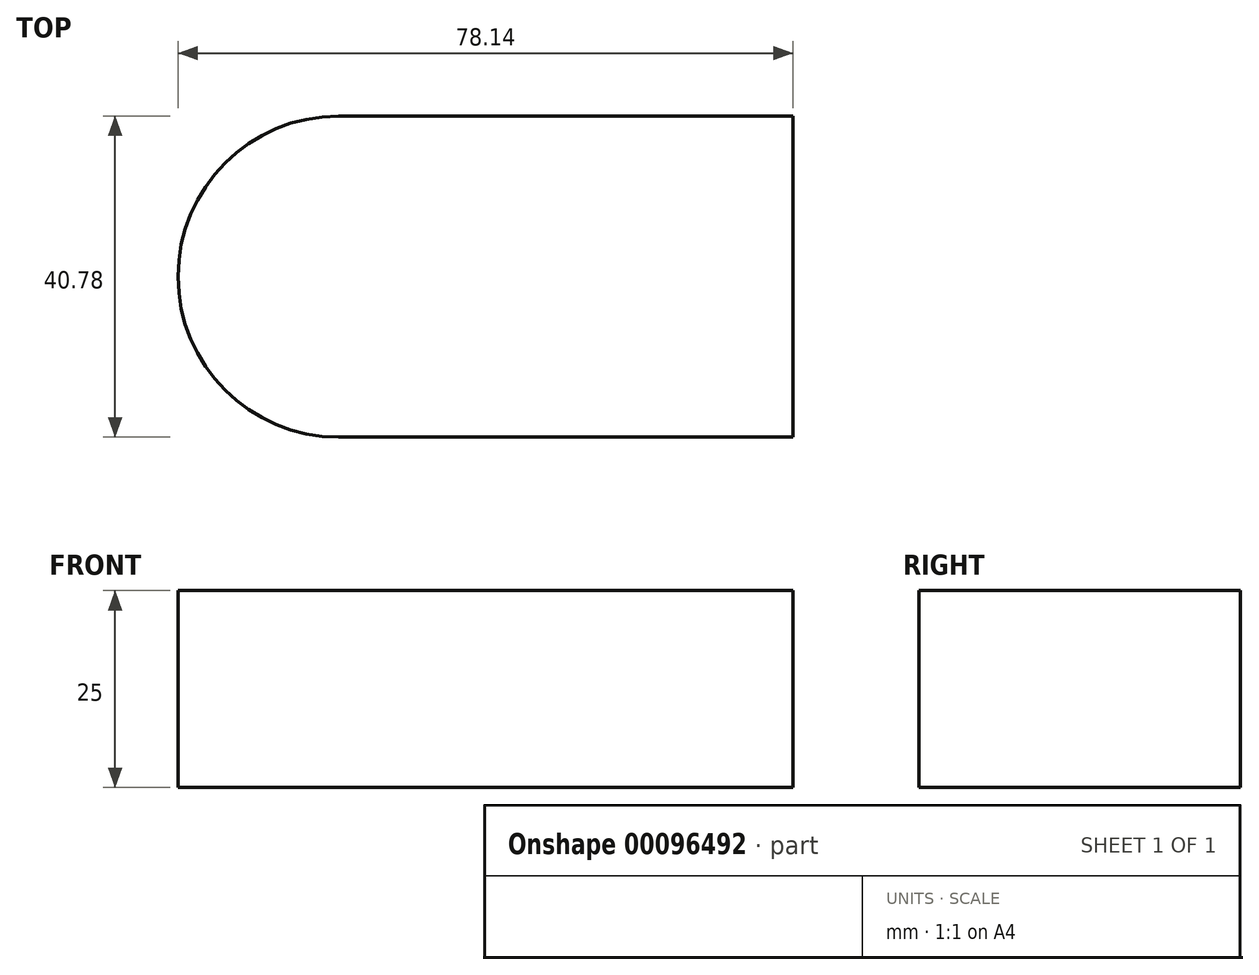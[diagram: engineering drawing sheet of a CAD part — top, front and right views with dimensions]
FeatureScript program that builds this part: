
annotation { "Feature Type Name" : "Feature", "Feature Type Description" : "" }
export const myFeature = defineFeature(function(context is Context, id is Id, definition is map)
    precondition{}
    {
        {
            var Q0;
            Q0=qCreatedBy(makeId("Top.planeOp"),FACE);
            var sketch = newSketch(context, id + "F0", { "sketchPlane" : qUnion([Q0])});
            skLineSegment(sketch, "E0.bottom", {"start": v(5, 0) * mm, "end": v(57.75, 0) * mm});
            skLineSegment(sketch, "E0.top", {"start": v(5, 40.78) * mm, "end": v(57.75, 40.78) * mm});
            skLineSegment(sketch, "E0.left", {"start": v(0, 5) * mm, "end": v(0, 35.78) * mm});
            skLineSegment(sketch, "E0.right", {"start": v(57.75, 0) * mm, "end": v(57.75, 40.78) * mm});
            skPoint(sketch, "E1.visualSharp", {"position": v(0, 0) * mm});
            skPoint(sketch, "E2.visualSharp", {"position": v(0, 40.78) * mm});
            skLineSegment(sketch, "E3", {"start": v(5, 40.78) * mm, "end": v(0, 40.78) * mm});
            skLineSegment(sketch, "E4", {"start": v(5, 0) * mm, "end": v(0, 0) * mm});
            skLineSegment(sketch, "E5", {"start": v(0, 5) * mm, "end": v(0, 40.78) * mm});
            skLineSegment(sketch, "E6", {"start": v(0, 5) * mm, "end": v(0, 0) * mm});
            skArc(sketch, "E7", {"start": v(0, 40.78) * mm, "mid": v(-20.39, 20.39) * mm, "end": v(0, 0) * mm});
            skSolve(sketch);
        }
        {
            var Q0;
            Q0 = qSketchRegion(id + "F0", true);
            extrude(context, id + "F1", {"entities" : qUnion([Q0]), "oppositeDirection" : true, "depth" : 25 * mm});
        }
    });
